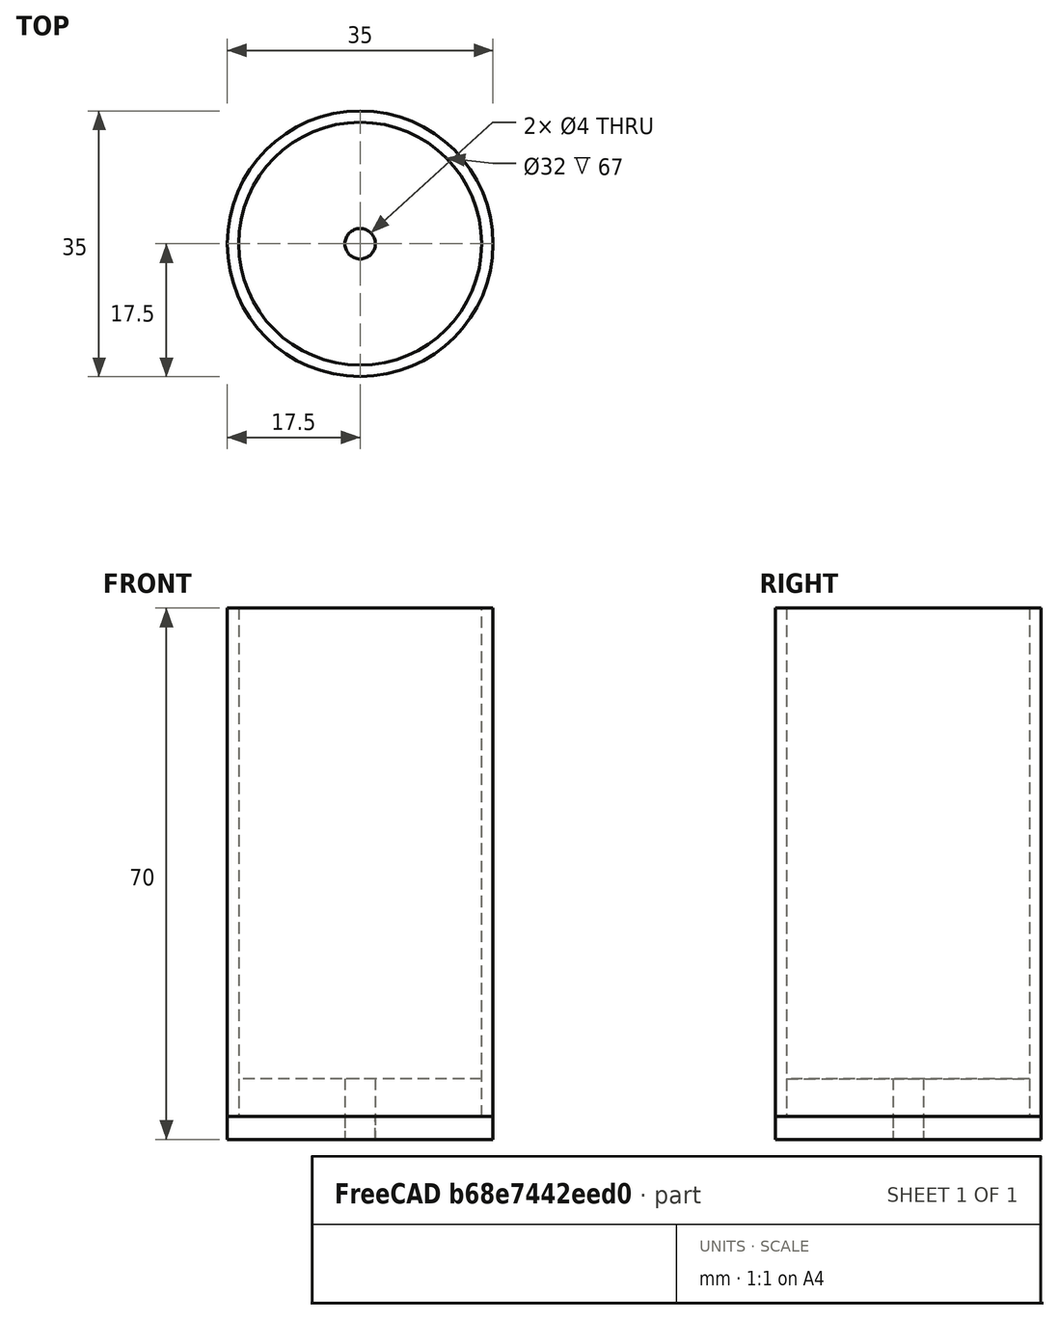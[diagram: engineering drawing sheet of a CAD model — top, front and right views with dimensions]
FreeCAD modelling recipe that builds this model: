
FCSTD DOCUMENT  (FreeCAD 1.0R38642 (Git))
Label: tube
License: All rights reserved
LicenseURL: https://en.wikipedia.org/wiki/All_rights_reserved
objects: PartDesign::Pad×4, PartDesign::Body×2, App::Link×2, App::FeaturePython×2, Spreadsheet::Sheet×1, Sketcher::SketchObject×1, PartDesign::SubShapeBinder×1, Assembly::JointGroup×1, Assembly::AssemblyObject×1
note: 17 computed .brp shape members not serialized (recipe doc carries the construction recipe); baked Part::Feature solids carry a one-line shape summary decoded from their .brp

FEATURE [Spreadsheet::Sheet] Spreadsheet  label="parameters"
  cells = A1='outer_diameter; B1(outer_diameter)==35 mm; A2='inner_diameter; B2(inner_diameter)==32 mm; A3='total_length; B3(total_length)==70 mm; A4='cap_height; B4(cap_height)==3 mm; A5='cap_recess_height; B5(cap_recess_height)==5 mm; A6='hole_diameter; B6(hole_diameter)==4 mm
FEATURE [Sketcher::SketchObject] Sketch
  ArcFitTolerance = 0
  AttachmentSupport = -> [XY_Plane]
  FullyConstrained = true
  MakeInternals = false
  MapMode = 5
  expr: Constraints[1] = <<parameters>>.outer_diameter
  expr: Constraints[3] = <<parameters>>.inner_diameter
  expr: Constraints[5] = <<parameters>>.hole_diameter
  sketch-geometry (3):
    g0: Circle CenterX=0 CenterY=0 CenterZ=0 NormalX=0 NormalY=0 NormalZ=1 AngleXU=0 Radius=17.5
    g1: Circle CenterX=0 CenterY=0 CenterZ=0 NormalX=0 NormalY=0 NormalZ=1 AngleXU=0 Radius=16
    g2: Circle CenterX=0 CenterY=0 CenterZ=0 NormalX=0 NormalY=0 NormalZ=1 AngleXU=0 Radius=2
  constraints (6):
    c: Coincident(g0,g-1)
    c: Diameter(g0) = 35
    c: Coincident(g1,g0)
    c: Diameter(g1) = 32
    c: Coincident(g2,g0)
    c: Diameter(g2) = 4
FEATURE [PartDesign::Pad] Pad  label="endcap"
  Direction = (0,0,1)
  Length = 3
  Length2 = 10
  Profile = -> Sketch [Edge3,Edge1]
  ReferenceAxis = -> Sketch [N_Axis]
  Refine = true
  Suppressed = false
  Type = 0
  expr: Length = <<parameters>>.cap_height
FEATURE [PartDesign::Pad] Pad001  label="walls"
  BaseFeature = -> Pad
  Direction = (0,0,1)
  Length = 70
  Length2 = 10
  Profile = -> Sketch [Edge1,Edge2]
  ReferenceAxis = -> Sketch [N_Axis]
  Refine = true
  Suppressed = false
  Type = 0
  expr: Length = <<parameters>>.total_length
FEATURE [PartDesign::Body] Body  label="case"
  AllowCompound = false
  Group = -> [Sketch,Pad,Pad001]
  Origin = -> Origin
  Tip = -> Pad001
FEATURE [PartDesign::SubShapeBinder] Binder
  BindCopyOnChange = 0
  BindMode = 0
  ClaimChildren = false
  Context = -> Body001 [Binder.]
  Fuse = false
  MakeFace = true
  OffsetFill = false
  OffsetIntersection = false
  OffsetJoinType = 0
  OffsetOpenResult = false
  PartialLoad = false
  Refine = true
  Relative = true
  Support = -> [Body[Sketch.]]
  _Version = 2
FEATURE [PartDesign::Pad] Pad002  label="recess"
  Direction = (0,0,1)
  Length = 8
  Length2 = 10
  Profile = -> Binder [Edge3,Edge2]
  Refine = true
  Suppressed = false
  Type = 0
  expr: Length = <<parameters>>.cap_recess_height + <<parameters>>.cap_height
FEATURE [PartDesign::Pad] Pad003  label="lip"
  BaseFeature = -> Pad002
  Direction = (0,0,1)
  Length = 3
  Length2 = 10
  Profile = -> Binder [Edge1,Edge3]
  Refine = true
  Suppressed = false
  Type = 0
  expr: Length = <<parameters>>.cap_height
FEATURE [PartDesign::Body] Body001  label="lid"
  AllowCompound = false
  Group = -> [Binder,Pad002,Pad003]
  Origin = -> Origin001
  Tip = -> Pad003
FEATURE [App::Link] case  label="case001"
  LinkPlacement = pos=(1.85373,-38.4224,0) rot=(0,0,1;0rad)
  LinkedObject = -> Body
  Placement = pos=(1.85373,-38.4224,0) rot=(0,0,1;0rad)
FEATURE [App::Link] lid  label="lid001"
  LinkedObject = -> Body001
FEATURE [App::FeaturePython] GroundedJoint  # Assembly grounded joint (typed FeaturePython)
  ObjectToGround = -> lid
FEATURE [App::FeaturePython] Distance  # Assembly joint (typed FeaturePython)
  Activated = true
  AngleMax = 0
  AngleMin = 0
  Detach1 = false
  Detach2 = false
  Distance = 0
  Distance2 = 0
  EnableAngleMax = false
  EnableAngleMin = false
  EnableLengthMax = false
  EnableLengthMin = false
  JointType = 5 (Distance)
  LengthMax = 0
  LengthMin = 0
  Offset = (0,0,0)
  Placement1 = pos=(-1.8e-15,0,0) rot=(0,0,1;0rad)
  Placement2 = pos=(-1.8e-15,-1e-15,0) rot=(0,0,1;0rad)
  Reference1 = -> Assembly [case.Pad001.Face5,case.Pad001.Face5]
  Reference2 = -> Assembly [lid.Pad003.Face5,lid.Pad003.Face5]
  Rotation = 0
FEATURE [Assembly::JointGroup] Joints
  Group = -> [GroundedJoint,Distance]
FEATURE [Assembly::AssemblyObject] Assembly
  Group = -> [Joints,case,lid,GroundedJoint,Distance]
  Origin = -> Origin002
  Type = Assembly
